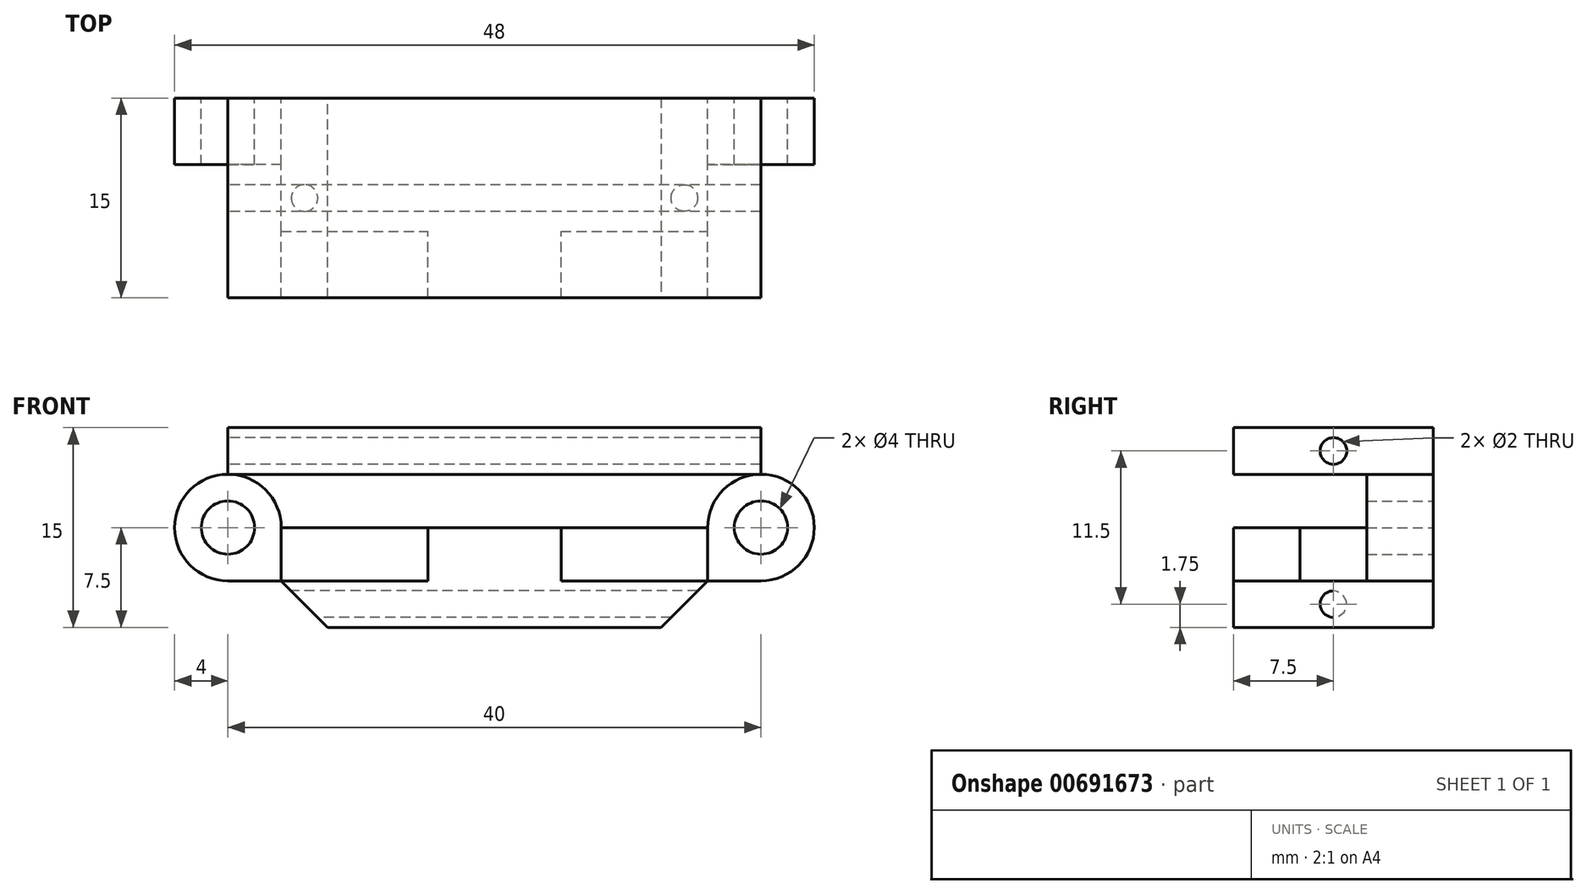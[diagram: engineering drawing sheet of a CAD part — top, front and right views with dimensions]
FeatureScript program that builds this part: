
annotation { "Feature Type Name" : "Feature", "Feature Type Description" : "" }
export const myFeature = defineFeature(function(context is Context, id is Id, definition is map)
    precondition{}
    {
        {
            var Q0;
            Q0=qCreatedBy(makeId("Front.planeOp"),FACE);
            var sketch = newSketch(context, id + "F0", { "sketchPlane" : qUnion([Q0])});
            skLineSegment(sketch, "E0.bottom", {"start": v(5, 4) * mm, "end": v(-5, 4) * mm});
            skLineSegment(sketch, "E0.top", {"start": v(5, -4) * mm, "end": v(-5, -4) * mm});
            skLineSegment(sketch, "E0.left", {"start": v(5, 4) * mm, "end": v(5, -4) * mm});
            skLineSegment(sketch, "E0.right", {"start": v(-5, 4) * mm, "end": v(-5, -4) * mm});
            skPoint(sketch, "E0.middle", {"position": v(0, 0) * mm});
            skLineSegment(sketch, "E1.bottom", {"start": v(-5, 4) * mm, "end": v(-20, 4) * mm});
            skLineSegment(sketch, "E1.top", {"start": v(-5, -4) * mm, "end": v(-20, -4) * mm});
            skLineSegment(sketch, "E1.right", {"start": v(-20, 4) * mm, "end": v(-20, -4) * mm});
            skLineSegment(sketch, "E2.bottom", {"start": v(5, 4) * mm, "end": v(20, 4) * mm});
            skLineSegment(sketch, "E2.top", {"start": v(5, -4) * mm, "end": v(20, -4) * mm});
            skLineSegment(sketch, "E2.right", {"start": v(20, 4) * mm, "end": v(20, -4) * mm});
            skCircle(sketch, "E3", {"center": v(-20, 0) * mm, "radius": 4 * mm});
            skCircle(sketch, "E4", {"center": v(-20, 0) * mm, "radius": 2 * mm});
            skCircle(sketch, "E5", {"center": v(20, 0) * mm, "radius": 4 * mm});
            skCircle(sketch, "E6", {"center": v(20, 0) * mm, "radius": 2 * mm});
            skLineSegment(sketch, "E7.bottom", {"start": v(-20, 4) * mm, "end": v(20, 4) * mm});
            skLineSegment(sketch, "E7.top", {"start": v(-20, 7.5) * mm, "end": v(20, 7.5) * mm});
            skLineSegment(sketch, "E7.left", {"start": v(-20, 4) * mm, "end": v(-20, 7.5) * mm});
            skLineSegment(sketch, "E7.right", {"start": v(20, 4) * mm, "end": v(20, 7.5) * mm});
            skLineSegment(sketch, "E8.bottom", {"start": v(-16, 0) * mm, "end": v(16, 0) * mm});
            skLineSegment(sketch, "E8.top", {"start": v(-16, -7.5) * mm, "end": v(16, -7.5) * mm});
            skLineSegment(sketch, "E8.left", {"start": v(-16, 0) * mm, "end": v(-16, -7.5) * mm});
            skLineSegment(sketch, "E8.right", {"start": v(16, 0) * mm, "end": v(16, -7.5) * mm});
            skSolve(sketch);
        }
        {
            var Q0;
            Q0=makeQuery(id+"F0.imprint","IMPRINT",FACE,{"disambiguationData":[TD([[makeQuery(id+"F0.imprint","IMPRINT",EDGE,{"derivedFrom":sQuery(id+"F0.wireOp",EDGE,"E7.top")}),-1.0]])]});
            var Q1;
            {var subQ0=sQuery(id+"F0.wireOp",EDGE,"E7.bottom");var subQ1=sQuery(id+"F0.wireOp",EDGE,"E0.right");var subQ2=makeQuery(id+"F0.imprint","INTERSECT",VERTEX,{"derivedFrom":[subQ1,subQ0]});Q1=makeQuery(id+"F0.imprint","IMPRINT",FACE,{"disambiguationData":[TD([[makeQuery(id+"F0.imprint","IMPRINT",EDGE,{"disambiguationData":[TD([[subQ2,-1.0]])],"derivedFrom":subQ1}),-1.0]])]});}
            var Q2;
            {var subQ1=sQuery(id+"F0.wireOp",EDGE,"E1.top");var subQ3=sQuery(id+"F0.wireOp",EDGE,"E8.left");var subQ4=makeQuery(id+"F0.imprint","INTERSECT",VERTEX,{"derivedFrom":[subQ1,subQ3]});Q2=makeQuery(id+"F0.imprint","IMPRINT",FACE,{"disambiguationData":[TD([[makeQuery(id+"F0.imprint","IMPRINT",EDGE,{"disambiguationData":[TD([[subQ4,1.0]])],"derivedFrom":subQ1}),-1.0]])]});}
            var Q3;
            {var subQ2=sQuery(id+"F0.wireOp",EDGE,"E0.top");Q3=makeQuery(id+"F0.imprint","IMPRINT",FACE,{"disambiguationData":[TD([[makeQuery(id+"F0.imprint","IMPRINT",EDGE,{"derivedFrom":subQ2}),1.0]])]});}
            var Q4;
            {var subQ0=sQuery(id+"F0.wireOp",EDGE,"E0.top");Q4=makeQuery(id+"F0.imprint","IMPRINT",FACE,{"disambiguationData":[TD([[makeQuery(id+"F0.imprint","IMPRINT",EDGE,{"derivedFrom":subQ0}),-1.0]])]});}
            var Q5;
            {var subQ0=sQuery(id+"F0.wireOp",EDGE,"E7.bottom");var subQ1=sQuery(id+"F0.wireOp",EDGE,"E0.right");var subQ2=makeQuery(id+"F0.imprint","INTERSECT",VERTEX,{"derivedFrom":[subQ1,subQ0]});Q5=makeQuery(id+"F0.imprint","IMPRINT",FACE,{"disambiguationData":[TD([[makeQuery(id+"F0.imprint","IMPRINT",EDGE,{"disambiguationData":[TD([[subQ2,-1.0]])],"derivedFrom":subQ1}),1.0]])]});}
            var Q6;
            {var subQ0=sQuery(id+"F0.wireOp",EDGE,"E7.bottom");var subQ1=sQuery(id+"F0.wireOp",EDGE,"E0.left");var subQ2=makeQuery(id+"F0.imprint","INTERSECT",VERTEX,{"derivedFrom":[subQ1,subQ0]});Q6=makeQuery(id+"F0.imprint","IMPRINT",FACE,{"disambiguationData":[TD([[makeQuery(id+"F0.imprint","IMPRINT",EDGE,{"disambiguationData":[TD([[subQ2,-1.0]])],"derivedFrom":subQ1}),1.0]])]});}
            var Q7;
            {var subQ1=sQuery(id+"F0.wireOp",EDGE,"E2.top");var subQ3=sQuery(id+"F0.wireOp",EDGE,"E8.right");var subQ4=makeQuery(id+"F0.imprint","INTERSECT",VERTEX,{"derivedFrom":[subQ1,subQ3]});Q7=makeQuery(id+"F0.imprint","IMPRINT",FACE,{"disambiguationData":[TD([[makeQuery(id+"F0.imprint","IMPRINT",EDGE,{"disambiguationData":[TD([[subQ4,1.0]])],"derivedFrom":subQ1}),1.0]])]});}
            extrude(context, id + "F1", {"entities" : qUnion([Q0, Q1, Q2, Q3, Q4, Q5, Q6, Q7]), "depth" : 10 * mm, "offsetDistance" : 25 * mm});
        }
        {
            var Q0;
            {var subQ1=sQuery(id+"F0.wireOp",EDGE,"E1.right");var subQ3=sQuery(id+"F0.wireOp",EDGE,"E4");var subQ4=makeQuery(id+"F0.imprint","INTERSECT",VERTEX,{"disambiguationData":[OD(0.0)],"derivedFrom":[subQ1,subQ3]});Q0=makeQuery(id+"F0.imprint","IMPRINT",FACE,{"disambiguationData":[TD([[makeQuery(id+"F0.imprint","IMPRINT",EDGE,{"disambiguationData":[TD([[subQ4,-1.0]])],"derivedFrom":subQ3}),-1.0]])]});}
            var Q1;
            {var subQ1=sQuery(id+"F0.wireOp",EDGE,"E1.right");var subQ4=sQuery(id+"F0.wireOp",EDGE,"E4");var subQ7=makeQuery(id+"F0.imprint","INTERSECT",VERTEX,{"disambiguationData":[OD(0.0)],"derivedFrom":[subQ1,subQ4]});Q1=makeQuery(id+"F0.imprint","IMPRINT",FACE,{"disambiguationData":[TD([[makeQuery(id+"F0.imprint","IMPRINT",EDGE,{"disambiguationData":[TD([[subQ7,1.0]])],"derivedFrom":subQ4}),-1.0]])]});}
            var Q2;
            {var subQ1=sQuery(id+"F0.wireOp",EDGE,"E1.top");var subQ3=sQuery(id+"F0.wireOp",EDGE,"E8.left");var subQ4=makeQuery(id+"F0.imprint","INTERSECT",VERTEX,{"derivedFrom":[subQ1,subQ3]});Q2=makeQuery(id+"F0.imprint","IMPRINT",FACE,{"disambiguationData":[TD([[makeQuery(id+"F0.imprint","IMPRINT",EDGE,{"disambiguationData":[TD([[subQ4,-1.0]])],"derivedFrom":subQ1}),-1.0]])]});}
            var Q3;
            {var subQ1=sQuery(id+"F0.wireOp",EDGE,"E2.top");var subQ3=sQuery(id+"F0.wireOp",EDGE,"E8.right");var subQ4=makeQuery(id+"F0.imprint","INTERSECT",VERTEX,{"derivedFrom":[subQ1,subQ3]});Q3=makeQuery(id+"F0.imprint","IMPRINT",FACE,{"disambiguationData":[TD([[makeQuery(id+"F0.imprint","IMPRINT",EDGE,{"disambiguationData":[TD([[subQ4,-1.0]])],"derivedFrom":subQ1}),1.0]])]});}
            var Q4;
            {var subQ1=sQuery(id+"F0.wireOp",EDGE,"E2.right");var subQ5=sQuery(id+"F0.wireOp",EDGE,"E6");var subQ7=makeQuery(id+"F0.imprint","INTERSECT",VERTEX,{"disambiguationData":[OD(0.0)],"derivedFrom":[subQ1,subQ5]});Q4=makeQuery(id+"F0.imprint","IMPRINT",FACE,{"disambiguationData":[TD([[makeQuery(id+"F0.imprint","IMPRINT",EDGE,{"disambiguationData":[TD([[subQ7,-1.0]])],"derivedFrom":subQ5}),-1.0]])]});}
            var Q5;
            {var subQ1=sQuery(id+"F0.wireOp",EDGE,"E2.right");var subQ3=sQuery(id+"F0.wireOp",EDGE,"E6");var subQ4=makeQuery(id+"F0.imprint","INTERSECT",VERTEX,{"disambiguationData":[OD(0.0)],"derivedFrom":[subQ1,subQ3]});Q5=makeQuery(id+"F0.imprint","IMPRINT",FACE,{"disambiguationData":[TD([[makeQuery(id+"F0.imprint","IMPRINT",EDGE,{"disambiguationData":[TD([[subQ4,1.0]])],"derivedFrom":subQ3}),-1.0]])]});}
            extrude(context, id + "F2", {"entities" : qUnion([Q0, Q1, Q2, Q3, Q4, Q5]), "operationType" : NewBodyOperationType.ADD, "depth" : 5 * mm, "offsetDistance" : 25 * mm});
        }
        {
            var Q0;
            {var subQ2=sQuery(id+"F0.wireOp",EDGE,"E0.top");Q0=makeQuery(id+"F0.imprint","IMPRINT",FACE,{"disambiguationData":[TD([[makeQuery(id+"F0.imprint","IMPRINT",EDGE,{"derivedFrom":subQ2}),1.0]])]});}
            var Q1;
            {var subQ0=sQuery(id+"F0.wireOp",EDGE,"E0.top");Q1=makeQuery(id+"F0.imprint","IMPRINT",FACE,{"disambiguationData":[TD([[makeQuery(id+"F0.imprint","IMPRINT",EDGE,{"derivedFrom":subQ0}),-1.0]])]});}
            var Q2;
            {var subQ0=sQuery(id+"F0.wireOp",EDGE,"E7.bottom");var subQ1=sQuery(id+"F0.wireOp",EDGE,"E0.right");var subQ2=makeQuery(id+"F0.imprint","INTERSECT",VERTEX,{"derivedFrom":[subQ1,subQ0]});Q2=makeQuery(id+"F0.imprint","IMPRINT",FACE,{"disambiguationData":[TD([[makeQuery(id+"F0.imprint","IMPRINT",EDGE,{"disambiguationData":[TD([[subQ2,-1.0]])],"derivedFrom":subQ1}),1.0]])]});}
            var Q3;
            Q3=makeQuery(id+"F0.imprint","IMPRINT",FACE,{"disambiguationData":[TD([[makeQuery(id+"F0.imprint","IMPRINT",EDGE,{"derivedFrom":sQuery(id+"F0.wireOp",EDGE,"E7.top")}),-1.0]])]});
            extrude(context, id + "F3", {"entities" : qUnion([Q0, Q1, Q2, Q3]), "operationType" : NewBodyOperationType.ADD, "depth" : 15 * mm, "offsetDistance" : 25 * mm});
        }
        {
            var Q0;
            {var subQ0=sQuery(id+"F0.wireOp",EDGE,"E7.left");Q0=makeQuery(id+"F3.boolean.opBoolean","MERGE",FACE,{"derivedFrom":[makeQuery(id+"F1.opExtrude","SWEPT_FACE",FACE,{"disambiguationData":[OSD([subQ0])]}),makeQuery(id+"F3.opExtrude","SWEPT_FACE",FACE,{"disambiguationData":[OSD([subQ0])]})]});}
            var sketch = newSketch(context, id + "F4", { "sketchPlane" : qUnion([Q0])});
            skLineSegment(sketch, "E9", {"start": v(7.5, 7.5) * mm, "end": v(7.5, -7.5) * mm});
            skLineSegment(sketch, "E10", {"start": v(7.5, 7.5) * mm, "end": v(7.5, 4) * mm});
            skLineSegment(sketch, "E11", {"start": v(7.5, -7.5) * mm, "end": v(7.5, -4) * mm});
            skCircle(sketch, "E12", {"center": v(7.5, -5.75) * mm, "radius": 1 * mm});
            skCircle(sketch, "E13", {"center": v(7.5, 5.75) * mm, "radius": 1 * mm});
            skSolve(sketch);
        }
        {
            var Q0;
            Q0 = qSketchRegion(id + "F4", true);
            extrude(context, id + "F5", {"entities" : qUnion([Q0]), "operationType" : NewBodyOperationType.REMOVE, "oppositeDirection" : true, "depth" : 40 * mm, "offsetDistance" : 25 * mm});
        }
        {
            var Q0;
            {var subQ0=sQuery(id+"F0.wireOp",EDGE,"E8.left");var subQ1=sQuery(id+"F0.wireOp",EDGE,"E8.top");Q0=makeQuery(id+"F3.boolean.opBoolean","MERGE",EDGE,{"derivedFrom":[makeQuery(id+"F1.opExtrude","SWEPT_EDGE",EDGE,{"disambiguationData":[OSD([subQ1,subQ0])]}),makeQuery(id+"F3.opExtrude","SWEPT_EDGE",EDGE,{"disambiguationData":[OSD([subQ1,subQ0])]})]});}
            var Q1;
            {var subQ0=sQuery(id+"F0.wireOp",EDGE,"E8.right");var subQ1=sQuery(id+"F0.wireOp",EDGE,"E8.top");Q1=makeQuery(id+"F3.boolean.opBoolean","MERGE",EDGE,{"derivedFrom":[makeQuery(id+"F1.opExtrude","SWEPT_EDGE",EDGE,{"disambiguationData":[OSD([subQ1,subQ0])]}),makeQuery(id+"F3.opExtrude","SWEPT_EDGE",EDGE,{"disambiguationData":[OSD([subQ1,subQ0])]})]});}
            chamfer(context, id + "F6", {"entities" : qUnion([Q0, Q1]), "width" : 3.5 * mm, "tangentPropagation" : true});
        }
    });
